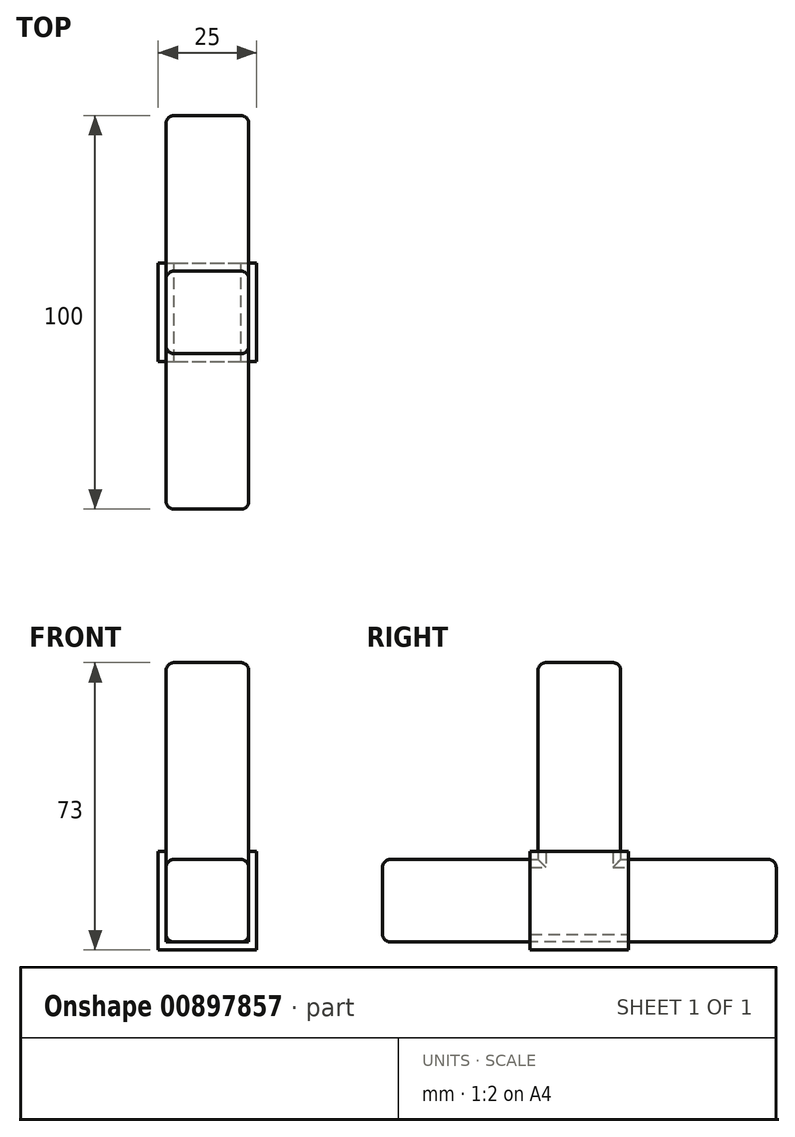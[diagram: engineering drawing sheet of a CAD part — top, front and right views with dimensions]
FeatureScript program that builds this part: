
annotation { "Feature Type Name" : "Feature", "Feature Type Description" : "" }
export const myFeature = defineFeature(function(context is Context, id is Id, definition is map)
    precondition{}
    {
        {
            var Q0;
            Q0=qCreatedBy(makeId("Front.planeOp"),FACE);
            var sketch = newSketch(context, id + "F0", { "sketchPlane" : qUnion([Q0])});
            skLineSegment(sketch, "E0.bottom", {"start": v(10.5, -10.5) * mm, "end": v(-10.5, -10.5) * mm});
            skLineSegment(sketch, "E0.top", {"start": v(10.5, 10.5) * mm, "end": v(-10.5, 10.5) * mm});
            skLineSegment(sketch, "E0.left", {"start": v(10.5, -10.5) * mm, "end": v(10.5, 10.5) * mm});
            skLineSegment(sketch, "E0.right", {"start": v(-10.5, -10.5) * mm, "end": v(-10.5, 10.5) * mm});
            skPoint(sketch, "E0.middle", {"position": v(0, 0) * mm});
            skSolve(sketch);
        }
        {
            var Q0;
            Q0 = qSketchRegion(id + "F0", true);
            extrude(context, id + "F1", {"entities" : qUnion([Q0]), "depth" : 100 * mm, "offsetDistance" : 25 * mm});
        }
        {
            var Q0;
            Q0=makeQuery(id+"F1.opExtrude","SWEPT_FACE",FACE,{"disambiguationData":[OSD([sQuery(id+"F0.wireOp",EDGE,"E0.top")])]});
            var sketch = newSketch(context, id + "F2", { "sketchPlane" : qUnion([Q0])});
            skLineSegment(sketch, "E1.bottom", {"start": v(10.5, -60.5) * mm, "end": v(-10.5, -60.5) * mm});
            skLineSegment(sketch, "E1.top", {"start": v(10.5, -39.5) * mm, "end": v(-10.5, -39.5) * mm});
            skLineSegment(sketch, "E1.left", {"start": v(10.5, -60.5) * mm, "end": v(10.5, -39.5) * mm});
            skLineSegment(sketch, "E1.right", {"start": v(-10.5, -60.5) * mm, "end": v(-10.5, -39.5) * mm});
            skPoint(sketch, "E1.middle", {"position": v(0, -50) * mm});
            skSolve(sketch);
        }
        {
            var Q0;
            Q0 = qSketchRegion(id + "F2", true);
            extrude(context, id + "F3", {"entities" : qUnion([Q0]), "operationType" : NewBodyOperationType.ADD, "depth" : 50 * mm, "offsetDistance" : 25 * mm});
        }
        {
            var Q0;
            Q0=makeQuery(id+"F1.opExtrude","SWEPT_EDGE",EDGE,{"disambiguationData":[OSD([sQuery(id+"F0.wireOp",EDGE,"E0.top"),sQuery(id+"F0.wireOp",EDGE,"E0.right")])]});
            var Q1;
            Q1=makeQuery(id+"F1.opExtrude","SWEPT_EDGE",EDGE,{"disambiguationData":[OSD([sQuery(id+"F0.wireOp",EDGE,"E0.top"),sQuery(id+"F0.wireOp",EDGE,"E0.left")])]});
            var Q2;
            Q2=makeQuery(id+"F1.opExtrude","SWEPT_EDGE",EDGE,{"disambiguationData":[OSD([sQuery(id+"F0.wireOp",EDGE,"E0.bottom"),sQuery(id+"F0.wireOp",EDGE,"E0.left")])]});
            var Q3;
            Q3=makeQuery(id+"F1.opExtrude","SWEPT_EDGE",EDGE,{"disambiguationData":[OSD([sQuery(id+"F0.wireOp",EDGE,"E0.bottom"),sQuery(id+"F0.wireOp",EDGE,"E0.right")])]});
            var Q4;
            Q4=makeQuery(id+"F1.opExtrude","CAP_EDGE",EDGE,{"disambiguationData":[OSD([sQuery(id+"F0.wireOp",EDGE,"E0.right")])],"isStart":false});
            var Q5;
            Q5=makeQuery(id+"F1.opExtrude","CAP_EDGE",EDGE,{"disambiguationData":[OSD([sQuery(id+"F0.wireOp",EDGE,"E0.top")])],"isStart":false});
            var Q6;
            Q6=makeQuery(id+"F1.opExtrude","CAP_EDGE",EDGE,{"disambiguationData":[OSD([sQuery(id+"F0.wireOp",EDGE,"E0.left")])],"isStart":false});
            var Q7;
            Q7=makeQuery(id+"F1.opExtrude","CAP_EDGE",EDGE,{"disambiguationData":[OSD([sQuery(id+"F0.wireOp",EDGE,"E0.bottom")])],"isStart":false});
            var Q8;
            Q8=makeQuery(id+"F1.opExtrude","CAP_EDGE",EDGE,{"disambiguationData":[OSD([sQuery(id+"F0.wireOp",EDGE,"E0.left")])],"isStart":true});
            var Q9;
            Q9=makeQuery(id+"F1.opExtrude","CAP_EDGE",EDGE,{"disambiguationData":[OSD([sQuery(id+"F0.wireOp",EDGE,"E0.top")])],"isStart":true});
            var Q10;
            Q10=makeQuery(id+"F1.opExtrude","CAP_EDGE",EDGE,{"disambiguationData":[OSD([sQuery(id+"F0.wireOp",EDGE,"E0.right")])],"isStart":true});
            var Q11;
            Q11=makeQuery(id+"F1.opExtrude","CAP_EDGE",EDGE,{"disambiguationData":[OSD([sQuery(id+"F0.wireOp",EDGE,"E0.bottom")])],"isStart":true});
            var Q12;
            Q12=makeQuery(id+"F3.opExtrude","SWEPT_EDGE",EDGE,{"disambiguationData":[OSD([sQuery(id+"F0.wireOp",EDGE,"E0.top"),sQuery(id+"F0.wireOp",EDGE,"E0.right"),sQuery(id+"F2.wireOp",EDGE,"E1.bottom"),sQuery(id+"F2.wireOp",EDGE,"E1.right")])]});
            var Q13;
            Q13=makeQuery(id+"F3.opExtrude","SWEPT_EDGE",EDGE,{"disambiguationData":[OSD([sQuery(id+"F0.wireOp",EDGE,"E0.top"),sQuery(id+"F0.wireOp",EDGE,"E0.left"),sQuery(id+"F2.wireOp",EDGE,"E1.bottom"),sQuery(id+"F2.wireOp",EDGE,"E1.left")])]});
            var Q14;
            Q14=makeQuery(id+"F3.opExtrude","CAP_EDGE",EDGE,{"disambiguationData":[OSD([sQuery(id+"F2.wireOp",EDGE,"E1.bottom")])],"isStart":false});
            var Q15;
            Q15=makeQuery(id+"F3.opExtrude","CAP_EDGE",EDGE,{"disambiguationData":[OSD([sQuery(id+"F2.wireOp",EDGE,"E1.left")])],"isStart":false});
            var Q16;
            Q16=makeQuery(id+"F3.opExtrude","CAP_EDGE",EDGE,{"disambiguationData":[OSD([sQuery(id+"F2.wireOp",EDGE,"E1.right")])],"isStart":false});
            var Q17;
            Q17=makeQuery(id+"F3.opExtrude","CAP_EDGE",EDGE,{"disambiguationData":[OSD([sQuery(id+"F2.wireOp",EDGE,"E1.top")])],"isStart":false});
            var Q18;
            Q18=makeQuery(id+"F3.opExtrude","SWEPT_EDGE",EDGE,{"disambiguationData":[OSD([sQuery(id+"F0.wireOp",EDGE,"E0.top"),sQuery(id+"F0.wireOp",EDGE,"E0.left"),sQuery(id+"F2.wireOp",EDGE,"E1.top"),sQuery(id+"F2.wireOp",EDGE,"E1.left")])]});
            var Q19;
            Q19=makeQuery(id+"F3.opExtrude","SWEPT_EDGE",EDGE,{"disambiguationData":[OSD([sQuery(id+"F0.wireOp",EDGE,"E0.top"),sQuery(id+"F0.wireOp",EDGE,"E0.right"),sQuery(id+"F2.wireOp",EDGE,"E1.top"),sQuery(id+"F2.wireOp",EDGE,"E1.right")])]});
            fillet(context, id + "F4", {"entities" : qUnion([Q0, Q1, Q2, Q3, Q4, Q5, Q6, Q7, Q8, Q9, Q10, Q11, Q12, Q13, Q14, Q15, Q16, Q17, Q18, Q19]), "radius" : 2 * mm, "tangentPropagation" : true, "allowEdgeOverflow" : false});
        }
        {
            var Q0;
            Q0=makeQuery(id+"F3.boolean.opBoolean","MERGE",FACE,{"derivedFrom":[makeQuery(id+"F1.opExtrude","SWEPT_FACE",FACE,{"disambiguationData":[OSD([sQuery(id+"F0.wireOp",EDGE,"E0.right")])]}),makeQuery(id+"F3.opExtrude","SWEPT_FACE",FACE,{"disambiguationData":[OSD([sQuery(id+"F2.wireOp",EDGE,"E1.right")])]})]});
            var sketch = newSketch(context, id + "F5", { "sketchPlane" : qUnion([Q0])});
            skLineSegment(sketch, "E2.0", {"start": v(2, 10.5) * mm, "end": v(39.5, 10.5) * mm});
            skLineSegment(sketch, "E3.0", {"start": v(60.5, 10.5) * mm, "end": v(98, 10.5) * mm});
            skLineSegment(sketch, "E4.bottom", {"start": v(39.5, 10.5) * mm, "end": v(60.5, 10.5) * mm, "construction": true});
            skLineSegment(sketch, "E4.top", {"start": v(39.5, -10.5) * mm, "end": v(60.5, -10.5) * mm, "construction": true});
            skLineSegment(sketch, "E4.left", {"start": v(39.5, 10.5) * mm, "end": v(39.5, -10.5) * mm, "construction": true});
            skLineSegment(sketch, "E4.right", {"start": v(60.5, 10.5) * mm, "end": v(60.5, -10.5) * mm});
            skLineSegment(sketch, "E5.0", {"start": v(37.5, 12.5) * mm, "end": v(62.5, 12.5) * mm});
            skLineSegment(sketch, "E5.1", {"start": v(37.5, 12.5) * mm, "end": v(37.5, -12.5) * mm});
            skLineSegment(sketch, "E5.2", {"start": v(37.5, -12.5) * mm, "end": v(62.5, -12.5) * mm});
            skLineSegment(sketch, "E5.3", {"start": v(62.5, 12.5) * mm, "end": v(62.5, -12.5) * mm});
            skSolve(sketch);
        }
        {
            var Q0;
            Q0 = qSketchRegion(id + "F5", true);
            extrude(context, id + "F6", {"entities" : qUnion([Q0]), "operationType" : NewBodyOperationType.ADD, "depth" : 2 * mm, "offsetDistance" : 25 * mm});
        }
        {
            var Q0;
            Q0=makeQuery(id+"F3.boolean.opBoolean","MERGE",FACE,{"derivedFrom":[makeQuery(id+"F1.opExtrude","SWEPT_FACE",FACE,{"disambiguationData":[OSD([sQuery(id+"F0.wireOp",EDGE,"E0.left")])]}),makeQuery(id+"F3.opExtrude","SWEPT_FACE",FACE,{"disambiguationData":[OSD([sQuery(id+"F2.wireOp",EDGE,"E1.left")])]})]});
            var sketch = newSketch(context, id + "F7", { "sketchPlane" : qUnion([Q0])});
            skLineSegment(sketch, "E6.0", {"start": v(-98, 10.5) * mm, "end": v(-60.5, 10.5) * mm, "construction": true});
            skLineSegment(sketch, "E7.0", {"start": v(-39.5, 10.5) * mm, "end": v(-2, 10.5) * mm, "construction": true});
            skLineSegment(sketch, "E8.bottom", {"start": v(-60.5, 10.5) * mm, "end": v(-39.5, 10.5) * mm, "construction": true});
            skLineSegment(sketch, "E8.top", {"start": v(-60.5, -10.5) * mm, "end": v(-39.5, -10.5) * mm, "construction": true});
            skLineSegment(sketch, "E8.left", {"start": v(-60.5, 10.5) * mm, "end": v(-60.5, -10.5) * mm, "construction": true});
            skLineSegment(sketch, "E8.right", {"start": v(-39.5, 10.5) * mm, "end": v(-39.5, -10.5) * mm, "construction": true});
            skLineSegment(sketch, "E9.0", {"start": v(-62.5, 12.5) * mm, "end": v(-37.5, 12.5) * mm});
            skLineSegment(sketch, "E9.1", {"start": v(-62.5, 12.5) * mm, "end": v(-62.5, -12.5) * mm});
            skLineSegment(sketch, "E9.2", {"start": v(-62.5, -12.5) * mm, "end": v(-37.5, -12.5) * mm});
            skLineSegment(sketch, "E9.3", {"start": v(-37.5, 12.5) * mm, "end": v(-37.5, -12.5) * mm});
            skSolve(sketch);
        }
        {
            var Q0;
            Q0 = qSketchRegion(id + "F7", true);
            extrude(context, id + "F8", {"entities" : qUnion([Q0]), "operationType" : NewBodyOperationType.ADD, "depth" : 2 * mm, "offsetDistance" : 25 * mm});
        }
        {
            var Q0;
            Q0=makeQuery(id+"F1.opExtrude","SWEPT_FACE",FACE,{"disambiguationData":[OSD([sQuery(id+"F0.wireOp",EDGE,"E0.bottom")])]});
            var sketch = newSketch(context, id + "F9", { "sketchPlane" : qUnion([Q0])});
            skLineSegment(sketch, "E10.0", {"start": v(-12.5, 37.5) * mm, "end": v(-12.5, 62.5) * mm});
            skLineSegment(sketch, "E11.0", {"start": v(12.5, 62.5) * mm, "end": v(12.5, 37.5) * mm});
            skLineSegment(sketch, "E12", {"start": v(-12.5, 62.5) * mm, "end": v(12.5, 62.5) * mm});
            skLineSegment(sketch, "E13", {"start": v(-12.5, 37.5) * mm, "end": v(12.5, 37.5) * mm});
            skSolve(sketch);
        }
        {
            var Q0;
            Q0 = qSketchRegion(id + "F9", true);
            extrude(context, id + "F10", {"entities" : qUnion([Q0]), "operationType" : NewBodyOperationType.ADD, "depth" : 2 * mm, "offsetDistance" : 25 * mm});
        }
    });
